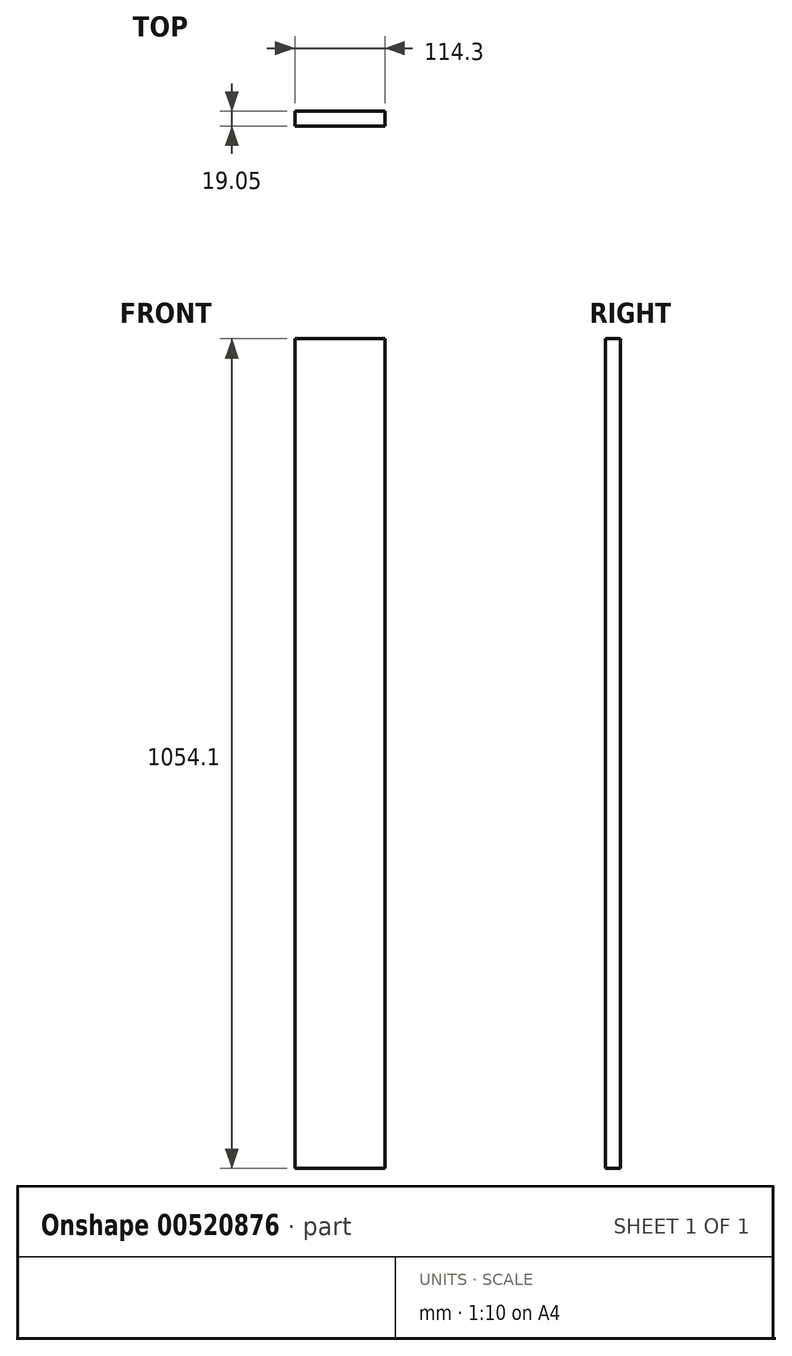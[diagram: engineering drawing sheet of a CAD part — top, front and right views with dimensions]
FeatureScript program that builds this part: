
annotation { "Feature Type Name" : "Feature", "Feature Type Description" : "" }
export const myFeature = defineFeature(function(context is Context, id is Id, definition is map)
    precondition{}
    {
        {
            var Q0;
            Q0=qCreatedBy(makeId("Front.planeOp"),FACE);
            var sketch = newSketch(context, id + "F0", { "sketchPlane" : qUnion([Q0])});
            skLineSegment(sketch, "E0.bottom", {"start": v(57.15, 527.05) * mm, "end": v(-57.15, 527.05) * mm});
            skLineSegment(sketch, "E0.top", {"start": v(57.15, -527.05) * mm, "end": v(-57.15, -527.05) * mm});
            skLineSegment(sketch, "E0.left", {"start": v(57.15, 527.05) * mm, "end": v(57.15, -527.05) * mm});
            skLineSegment(sketch, "E0.right", {"start": v(-57.15, 527.05) * mm, "end": v(-57.15, -527.05) * mm});
            skPoint(sketch, "E0.middle", {"position": v(0, 0) * mm});
            skSolve(sketch);
        }
        {
            var Q0;
            Q0=makeQuery(id+"F0.imprint","IMPRINT",FACE,{"disambiguationData":[TD([[makeQuery(id+"F0.imprint","IMPRINT",EDGE,{"derivedFrom":sQuery(id+"F0.wireOp",EDGE,"E0.bottom")}),1.0]])]});
            extrude(context, id + "F1", {"entities" : qUnion([Q0]), "depth" : 19.05 * mm, "offsetDistance" : 25.4 * mm});
        }
    });
